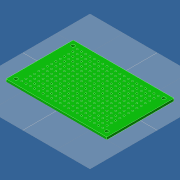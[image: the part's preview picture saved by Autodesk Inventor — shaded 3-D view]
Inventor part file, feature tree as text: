
AUTODESK INVENTOR PART (.ipt)
format: ipt  version: 2016 SP2 (Build 200236200, 236)  size: 356,864 bytes
history: native  units: mm
features: sketch x2, extrude x2, hole x1
ambient origin geometry x8: Origin, YZ Plane, XZ Plane, XY Plane, X Axis, Y Axis, Z Axis, Center Point
bodies: Volumenkörper1 (feature_tree)
feature tree (5):
  sketch  "Skizze1"  dims[d0=60.0mm d1=40.0mm]
  extrude  "Extrusion1"  Depth=40.0mm
  hole  "Bohrung1"  [1 undecoded]
  extrude  "Extrusion2"  Depth=1.5mm
  sketch  "Skizze2"  dims[d2=1.5mm d3=0.0mm d4=2.54mm d5=2.54mm d6=70.0mm d8=2.54mm d9=100.0mm d11=2.54mm d14=100.0mm d16=2.54mm d17=70.0mm d19=2.54mm d22=70.0mm d24=2.54mm d25=100.0mm d27=2.54mm d30=70.0mm d32=2.54mm d33=100.0mm d35=2.54mm d38=1.0mm d39=6.0mm d40=4.0mm d41=2.0mm d42=90.0deg d43=8.0mm d44=20.594885mm d45=2.0mm d46=54.0mm d47=34.0mm d48=1.5mm d49=0.0mm]
note: 1 required parameter value undecoded (feature->parameter linkage not recoverable at this tier; creation-order binding heuristic only, values carry confidence <= 0.55)
